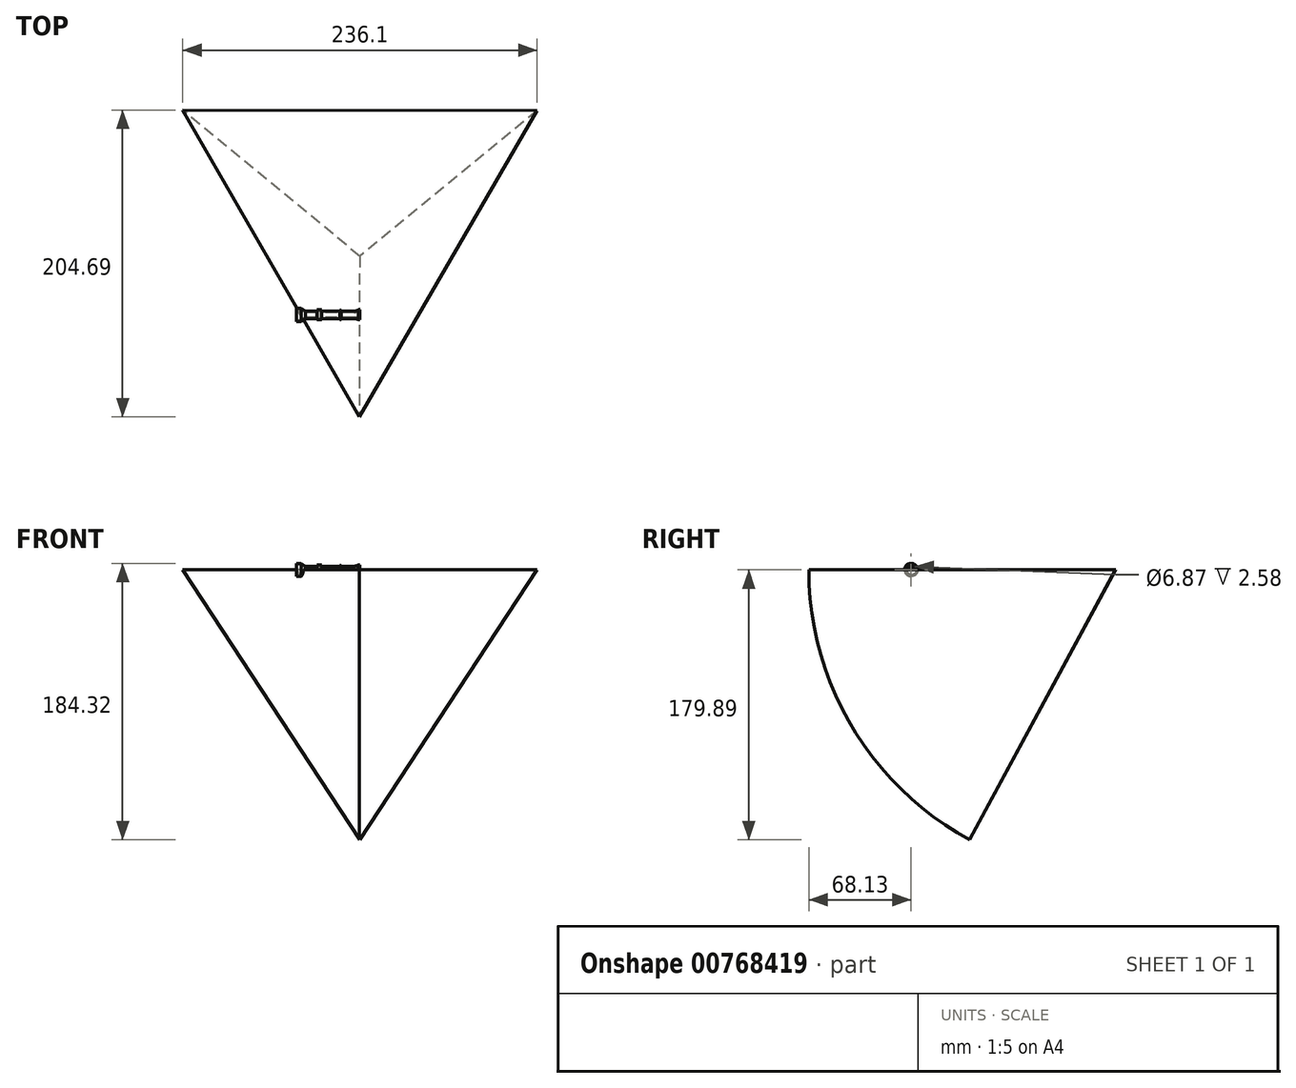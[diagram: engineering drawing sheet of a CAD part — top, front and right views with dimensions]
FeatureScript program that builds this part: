
annotation { "Feature Type Name" : "Feature", "Feature Type Description" : "" }
export const myFeature = defineFeature(function(context is Context, id is Id, definition is map)
    precondition{}
    {
        {
            var Q0;
            Q0=qCreatedBy(makeId("Front.planeOp"),FACE);
            var sketch = newSketch(context, id + "F0", { "sketchPlane" : qUnion([Q0])});
            skLineSegment(sketch, "E0", {"start": v(-42, 0) * mm, "end": v(0, 0) * mm, "construction": true});
            skLineSegment(sketch, "E1", {"start": v(-42, 0) * mm, "end": v(-42, 4.43) * mm});
            skLineSegment(sketch, "E2", {"start": v(-42, 4.43) * mm, "end": v(-39.11, 4.43) * mm});
            skLineSegment(sketch, "E3", {"start": v(-39.11, 4.43) * mm, "end": v(-36.25, 2.5) * mm});
            skLineSegment(sketch, "E4", {"start": v(-36.25, 2.5) * mm, "end": v(-28.48, 2.5) * mm});
            skLineSegment(sketch, "E5", {"start": v(-28.48, 2.5) * mm, "end": v(-28.48, 3.31) * mm});
            skLineSegment(sketch, "E6", {"start": v(-28.48, 3.31) * mm, "end": v(-25.4, 3.31) * mm});
            skLineSegment(sketch, "E7", {"start": v(-25.4, 3.31) * mm, "end": v(-25.4, 2.5) * mm});
            skLineSegment(sketch, "E8", {"start": v(-25.4, 2.5) * mm, "end": v(-13.17, 2.5) * mm});
            skLineSegment(sketch, "E9", {"start": v(-0.94, 2.5) * mm, "end": v(-0.94, 3.31) * mm});
            skLineSegment(sketch, "E10", {"start": v(-0.94, 3.31) * mm, "end": v(0, 3.31) * mm});
            skLineSegment(sketch, "E11", {"start": v(0, 3.31) * mm, "end": v(0, 0) * mm});
            skLineSegment(sketch, "E12", {"start": v(-13.17, 2.5) * mm, "end": v(-13.17, 3.12) * mm});
            skLineSegment(sketch, "E13", {"start": v(-13.17, 3.12) * mm, "end": v(-12.32, 3.12) * mm});
            skLineSegment(sketch, "E14", {"start": v(-12.32, 3.12) * mm, "end": v(-12.32, 2.5) * mm});
            skLineSegment(sketch, "E15.trimOffspring", {"start": v(-12.32, 2.5) * mm, "end": v(-0.94, 2.5) * mm});
            skLineSegment(sketch, "E16", {"start": v(-42, 0) * mm, "end": v(0, 0) * mm});
            skSolve(sketch);
        }
        {
            var Q0;
            Q0=makeQuery(id+"F0.imprint","IMPRINT",FACE,{"disambiguationData":[TD([[makeQuery(id+"F0.imprint","IMPRINT",EDGE,{"derivedFrom":sQuery(id+"F0.wireOp",EDGE,"E1")}),-1.0]])]});
            var Q1;
            Q1=sQuery(id+"F0.wireOp",EDGE,"E16");
            revolve(context, id + "F1", {"entities" : qUnion([Q0]), "axis" : qUnion([Q1]), "revolveType" : RevolveType.FULL});
        }
        {
            var Q0;
            Q0=qCreatedBy(makeId("Top.planeOp"),FACE);
            var sketch = newSketch(context, id + "F2", { "sketchPlane" : qUnion([Q0])});
            skCircle(sketch, "E17", {"center": v(-14.84, 0) * mm, "radius": 1.5 * mm});
            skSolve(sketch);
        }
        {
            var Q0;
            Q0=qSketchRegion(id+"F2",true);
            extrude(context, id + "F3", {"entities" : qUnion([Q0]), "operationType" : NewBodyOperationType.ADD, "oppositeDirection" : true, "depth" : 8 * mm});
        }
        {
            var Q0;
            Q0=makeQuery(id+"F1.opRevolve","SWEPT_EDGE",EDGE,{"disambiguationData":[OSD([sQuery(id+"F0.wireOp",EDGE,"E9"),sQuery(id+"F0.wireOp",EDGE,"E15.trimOffspring")])]});
            fillet(context, id + "F4", {"entities" : qUnion([Q0]), "radius" : 5 * mm, "tangentPropagation" : true, "allowEdgeOverflow" : false});
        }
        {
            var Q0;
            Q0=makeQuery(id+"F1.opRevolve","SWEPT_FACE",FACE,{"disambiguationData":[OSD([sQuery(id+"F0.wireOp",EDGE,"E1")])]});
            var Q1;
            Q1=makeQuery(id+"F1.opRevolve","SWEPT_FACE",FACE,{"disambiguationData":[OSD([sQuery(id+"F0.wireOp",EDGE,"E11")])]});
            shell(context, id + "F5", {"entities" : qUnion([Q0, Q1]), "thickness" : 1 * mm});
        }
        {
            var Q0;
            Q0=qCreatedBy(makeId("Top.planeOp"),FACE);
            var sketch = newSketch(context, id + "F6", { "sketchPlane" : qUnion([Q0])});
            skCircle(sketch, "E18.cCircle", {"center": v(0, 68.19) * mm, "radius": 68.16 * mm, "construction": true});
            skLineSegment(sketch, "E18.0", {"start": v(118.17, 136.14) * mm, "end": v(-0.24, -68.13) * mm});
            skLineSegment(sketch, "E18.1", {"start": v(-0.24, -68.13) * mm, "end": v(-117.93, 136.56) * mm});
            skLineSegment(sketch, "E18.2", {"start": v(-117.93, 136.56) * mm, "end": v(118.17, 136.14) * mm});
            skPoint(sketch, "E18.0.midPoint", {"position": v(58.97, 34) * mm});
            skSolve(sketch);
        }
        {
            var Q0;
            Q0=makeQuery(id+"F6.imprint","IMPRINT",FACE,{"disambiguationData":[TD([[makeQuery(id+"F6.imprint","IMPRINT",EDGE,{"derivedFrom":sQuery(id+"F6.wireOp",EDGE,"E18.0")}),-1.0]])]});
            var Q1;
            Q1=sQuery(id+"F6.wireOp",EDGE,"E18.2");
            revolve(context, id + "F7", {"operationType" : NewBodyOperationType.ADD, "surfaceOperationType" : NewSurfaceOperationType.NEW, "entities" : qUnion([Q0]), "axis" : qUnion([Q1]), "revolveType" : RevolveType.ONE_DIRECTION, "angle" : 61.62 * degree});
        }
    });
